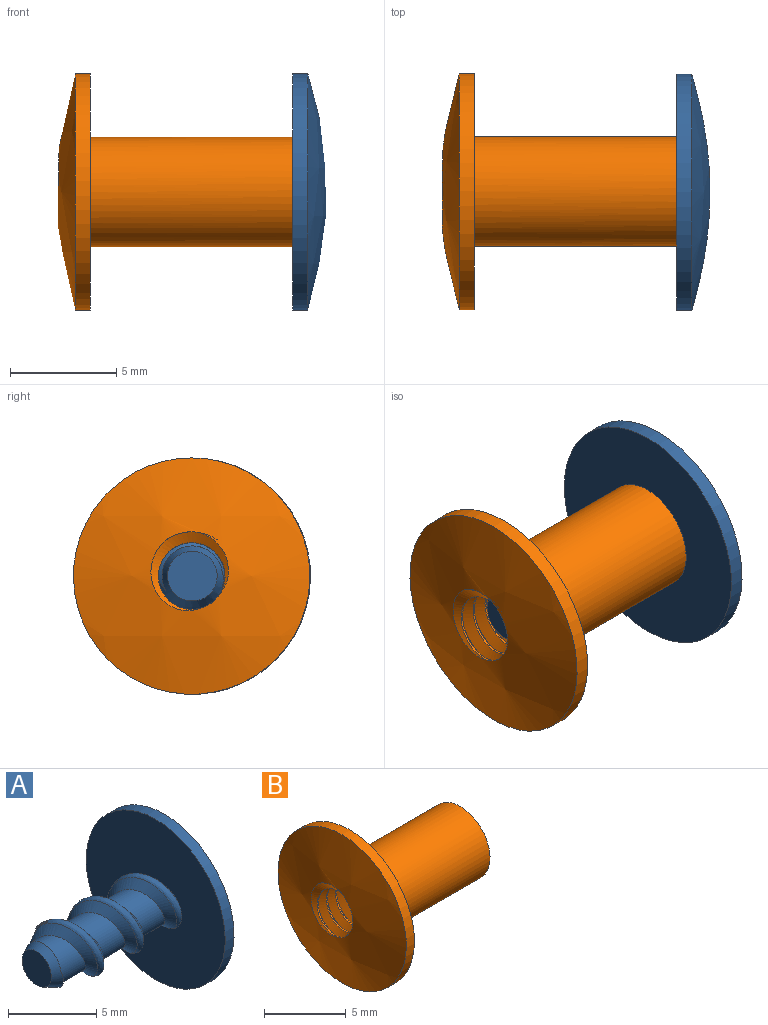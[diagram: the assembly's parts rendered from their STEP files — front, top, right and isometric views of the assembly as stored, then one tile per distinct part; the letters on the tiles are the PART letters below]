
ASSEMBLY  parts=2 mates=1
PART A: 9 faces, bbox 11.2x11.3x11.3 mm
  f0: cone r=1.17mm half-angle=25deg, axis (1,0,0), area 9.3mm2, adj f1,f5,f6,f7,f8
  f1: cylinder r=1.42mm len=8.98mm, axis (-1,0,0), area 44.4mm2, adj f0,f4,f5,f6
  f2: cylinder r=5.56mm len=11.11mm, axis (-1,0,0), area 24.6mm2, adj f3,f4
  f3: sphere r=17.94mm, area 99.4mm2, adj f2
  f4: plane 11.23x11.23mm, normal (-1,0,0), area 88.8mm2, adj f1,f2,f5,f6,f7
  f5: bspline ~9.89x3.92mm, area 20.4mm2, adj f0,f1,f4,f7
  f6: bspline ~9.44x3.93mm, area 20.4mm2, adj f0,f1,f4,f7
  f7: bspline ~8.83x4.16mm, area 18.4mm2, adj f0,f4,f5,f6
  f8: plane 2.34x2.34mm, normal (-1,0,0), area 4.3mm2, adj f0
PART B: 10 faces, bbox 11.6x11.1x11.2 mm
  f0: cylinder r=5.56mm len=11.11mm, axis (1,0,0), area 24.6mm2, adj f2,f9
  f1: cone r=2.08mm half-angle=45deg, axis (1,0,0), area 4.3mm2, adj f4,f5,f6,f7,f8
  f2: sphere r=17.94mm, area 89.1mm2, adj f0,f4,f5,f6,f7
  f3: cylinder r=2.58mm len=9.53mm, axis (1,0,0), area 154.3mm2, adj f8,f9
  f4: cylinder r=2.08mm len=10.99mm, axis (1,0,0), area 18mm2, adj f1,f2,f5,f6,f8
  f5: bspline ~11.61x4.17mm, area 92.3mm2, adj f1,f2,f4,f7
  f6: bspline ~11.31x4.17mm, area 92.8mm2, adj f1,f2,f4,f7
  f7: cylinder r=1.57mm len=10.53mm, axis (-1,0,0), area 12.9mm2, adj f1,f2,f5,f6
  f8: plane 5.16x5.16mm, normal (1,0,0), area 7.3mm2, adj f1,f3,f4
  f9: plane 11.11x11.11mm, normal (1,0,0), area 76.1mm2, adj f0,f3
PLACE A at identity
PLACE B t=(15.88,0.03,0.01)mm
MATE fastened B.f1 <-> A.f4  axis (1,0,0) through (9.53,0.03,0.01)mm
